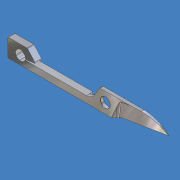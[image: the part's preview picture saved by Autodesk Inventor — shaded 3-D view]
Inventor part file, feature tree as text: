
AUTODESK INVENTOR PART (.ipt)
format: ipt  version: unknown  size: 293,888 bytes
history: native  units: mm (DEFAULTED — no unit token found)
features: sketch x7, fillet x7, extrude x5, other x2, plane x1, chamfer x1
ambient origin geometry x8: Origin, YZ Plane, XZ Plane, XY Plane, X Axis, Y Axis, Z Axis, Center Point
feature tree (23):
  extrude  "Extrusion1"  Depth=50.0mm
  extrude  "Extrusion2"  Depth=3.0mm
  sketch  "Sketch4"  dims[d7=11.0mm d8=2.0mm]
  other  "Work Point2"
  other  "Work Point3"
  sketch  "Sketch8"  dims[d9=6.0mm d10=2.0mm d11=0.0mm d12=2.0mm d13=0.0mm d26=0.4mm d27=5.0mm d28=10.0mm d29=0.0mm d34=9.0mm d35=3.0mm]
  plane  "Work Plane6"
  extrude  "Extrusion5"  Depth=2.0mm
  extrude  "Extrusion6"  Depth=2.0mm TaperAngle=0.0deg
  fillet  "Fillet3"  Radius=2.0mm
  fillet  "Fillet5"  Radius=0.4mm
  fillet  "Fillet6"  Radius=5.0mm
  fillet  "Fillet8"  Radius=10.0mm
  fillet  "Fillet9"  Radius=9.0mm
  fillet  "Fillet10"  Radius=3.0mm
  extrude  "Extrusion8"  Depth=2.6mm
  fillet  "Fillet11"  Radius=10.0mm
  chamfer  "Chamfer3"  Distance=3.0mm
  sketch  "Sketch1"  dims[d3=2.9mm d4=50.0mm]
  sketch  "Sketch2"  dims[d5=29.5mm d6=3.0mm]
  sketch  "Sketch9"  dims[d36=3.8mm d37=2.6mm d38=10.0mm d39=0.0mm]
  sketch  "Sketch10"  dims[d40=0.2mm]
  sketch  "Sketch12"  dims[d42=0.2mm d43=3.0mm d44=20.5mm d45=120.0deg d46=4.0mm d50=3.0mm d52=75.0deg d54=45.0deg d56=0.25mm d57=1.0mm d58=0.25mm d59=15.0mm d60=0.5mm d61=23.5mm d62=15.5mm d63=1.6mm d64=6.5mm d65=10.0mm d66=0.0mm d67=0.2mm d68=0.1mm d69=0.1mm d70=45.0deg]
